# Revit family: CELC-Surface
name_source: partatom
category: Lighting Fixtures
revit_build: Autodesk Revit 2014 (Build: 20130308_1515(x64)
units: mm (PartAtom-declared; Revit-internal decimal feet)

## types (1)
- CELC
    Apparent Load = 4 VA
    Certification = UL924 Listed for Damp Location
• NFPA 101
• NFPA 70
• OSHA
• CEC T20 Compliant
    Default Elevation = 48.000"
    Description = The CELEM Series is a recessed architectural LED based Emergency Light with adjustable LED lamps
    Double Face = No
    Features = Superior panel illumination with 6 inch Red or Green letters
• LED life-cycle exceeding 10 years
• Battery re-charge within 24 hours
• Damp location listed 10°C to 40°C (50°F to 104°F)
• Dual-voltage 120 or 277V AC, 60 Hz. input
• Includes long-life Nickel Metal Hydride battery for UL recognized 90
minute emergency lighting
• Pre-installed directional arrow indicator with template
• Provided with test switch and AC-On indicator
• Canopy included for surface mount model
• Matching CELEM Recessed emergency light
    Finish = Hubbell - White
    Glass = Hubbell - light Glass
    Holder Material = Hubbell - Steel
    Lamp = LED Lamp
    Length = 16.720"
    Lens = Hubbell Light Yellow
    Load Classification = Lighting
    Manufacturer = Compass Lighting
    Model = CELC
    Product Documentation Link = https://hubbellcdn.com
    Product Page URL = https://www.hubbell.com
    Sign = Hubbell - Red Glass
    Single Face = Yes
    Type Comments = Exit Light
    URL = https://www.hubbell.com
    Wall Plate Material = Hubbell - Black
    Warranty = 2 year full unit warranty
    Wattage Comments = 3.72 W
    Watts = 4 W
    Width = 2.063"

## geometry (parser evidence)
native form markers: Blend x8, Sweep x5
no freeform markers — native parametric forms only
